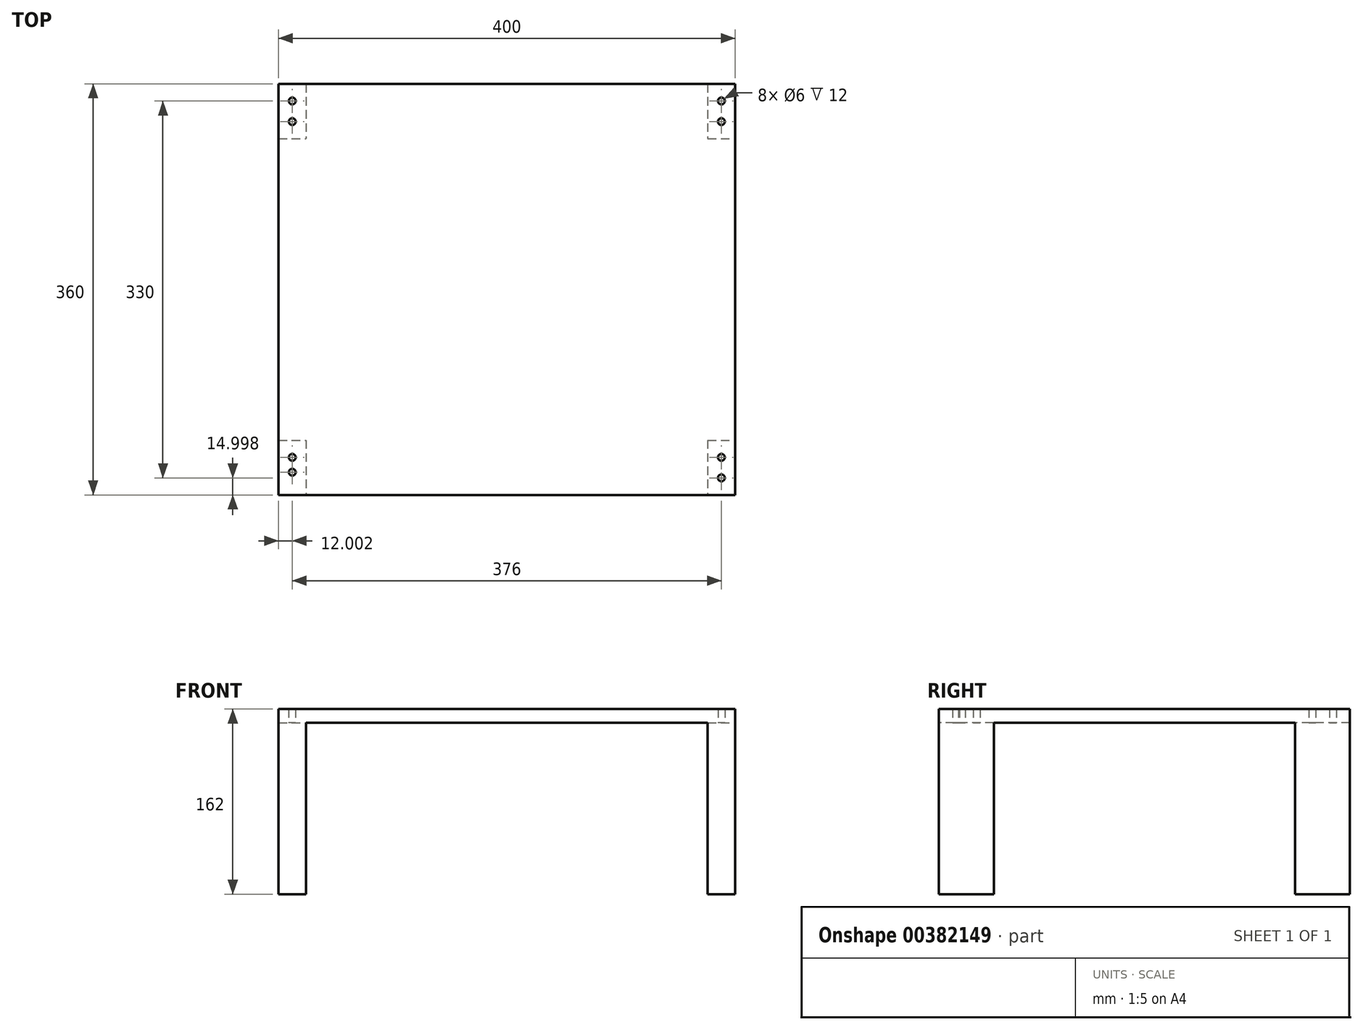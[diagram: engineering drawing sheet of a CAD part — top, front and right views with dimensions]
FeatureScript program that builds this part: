
annotation { "Feature Type Name" : "Feature", "Feature Type Description" : "" }
export const myFeature = defineFeature(function(context is Context, id is Id, definition is map)
    precondition{}
    {
        {
            var Q0;
            Q0=qCreatedBy(makeId("Top.planeOp"),FACE);
            var sketch = newSketch(context, id + "F0", { "sketchPlane" : qUnion([Q0])});
            skLineSegment(sketch, "E0.bottom", {"start": v(-230.97, 131.75) * mm, "end": v(169.03, 131.75) * mm});
            skLineSegment(sketch, "E0.top", {"start": v(-230.97, -228.25) * mm, "end": v(169.03, -228.25) * mm});
            skLineSegment(sketch, "E0.left", {"start": v(-230.97, 131.75) * mm, "end": v(-230.97, -228.25) * mm});
            skLineSegment(sketch, "E0.right", {"start": v(169.03, 131.75) * mm, "end": v(169.03, -228.25) * mm});
            skCircle(sketch, "E1", {"center": v(-218.97, -208.25) * mm, "radius": 3 * mm});
            skCircle(sketch, "E2", {"center": v(-218.97, -195.25) * mm, "radius": 3 * mm});
            skCircle(sketch, "E3", {"center": v(157.03, -213.25) * mm, "radius": 3 * mm});
            skCircle(sketch, "E4", {"center": v(157.03, -195.25) * mm, "radius": 3 * mm});
            skCircle(sketch, "E5", {"center": v(157.03, 98.75) * mm, "radius": 3 * mm});
            skCircle(sketch, "E6", {"center": v(157.03, 116.75) * mm, "radius": 3 * mm});
            skCircle(sketch, "E7", {"center": v(-218.97, 98.75) * mm, "radius": 3 * mm});
            skCircle(sketch, "E8", {"center": v(-218.97, 116.75) * mm, "radius": 3 * mm});
            skSolve(sketch);
        }
        {
            var Q0;
            Q0=qCreatedBy(makeId("Top.planeOp"),FACE);
            var sketch = newSketch(context, id + "F1", { "sketchPlane" : qUnion([Q0])});
            skLineSegment(sketch, "E9.bottom", {"start": v(-230.97, -180.25) * mm, "end": v(-206.97, -180.25) * mm});
            skLineSegment(sketch, "E9.top", {"start": v(-230.97, -228.25) * mm, "end": v(-206.97, -228.25) * mm});
            skLineSegment(sketch, "E9.left", {"start": v(-230.97, -180.25) * mm, "end": v(-230.97, -228.25) * mm});
            skLineSegment(sketch, "E9.right", {"start": v(-206.97, -180.25) * mm, "end": v(-206.97, -228.25) * mm});
            skLineSegment(sketch, "E10.bottom", {"start": v(-230.97, 131.75) * mm, "end": v(-206.97, 131.75) * mm});
            skLineSegment(sketch, "E10.top", {"start": v(-230.97, 83.75) * mm, "end": v(-206.97, 83.75) * mm});
            skLineSegment(sketch, "E10.left", {"start": v(-230.97, 131.75) * mm, "end": v(-230.97, 83.75) * mm});
            skLineSegment(sketch, "E10.right", {"start": v(-206.97, 131.75) * mm, "end": v(-206.97, 83.75) * mm});
            skLineSegment(sketch, "E11.bottom", {"start": v(145.03, 131.75) * mm, "end": v(169.03, 131.75) * mm});
            skLineSegment(sketch, "E11.top", {"start": v(145.03, 83.75) * mm, "end": v(169.03, 83.75) * mm});
            skLineSegment(sketch, "E11.left", {"start": v(145.03, 131.75) * mm, "end": v(145.03, 83.75) * mm});
            skLineSegment(sketch, "E11.right", {"start": v(169.03, 131.75) * mm, "end": v(169.03, 83.75) * mm});
            skLineSegment(sketch, "E12.bottom", {"start": v(145.03, -180.25) * mm, "end": v(169.03, -180.25) * mm});
            skLineSegment(sketch, "E12.top", {"start": v(145.03, -228.25) * mm, "end": v(169.03, -228.25) * mm});
            skLineSegment(sketch, "E12.left", {"start": v(145.03, -180.25) * mm, "end": v(145.03, -228.25) * mm});
            skLineSegment(sketch, "E12.right", {"start": v(169.03, -180.25) * mm, "end": v(169.03, -228.25) * mm});
            skSolve(sketch);
        }
        {
            var Q0;
            Q0=qSketchRegion(id+"F0",true);
            extrude(context, id + "F2", {"entities" : qUnion([Q0]), "depth" : 12 * mm});
        }
        {
            var Q0;
            Q0=qSketchRegion(id+"F1",true);
            extrude(context, id + "F3", {"entities" : qUnion([Q0]), "operationType" : NewBodyOperationType.ADD, "depth" : -150 * mm});
        }
    });
